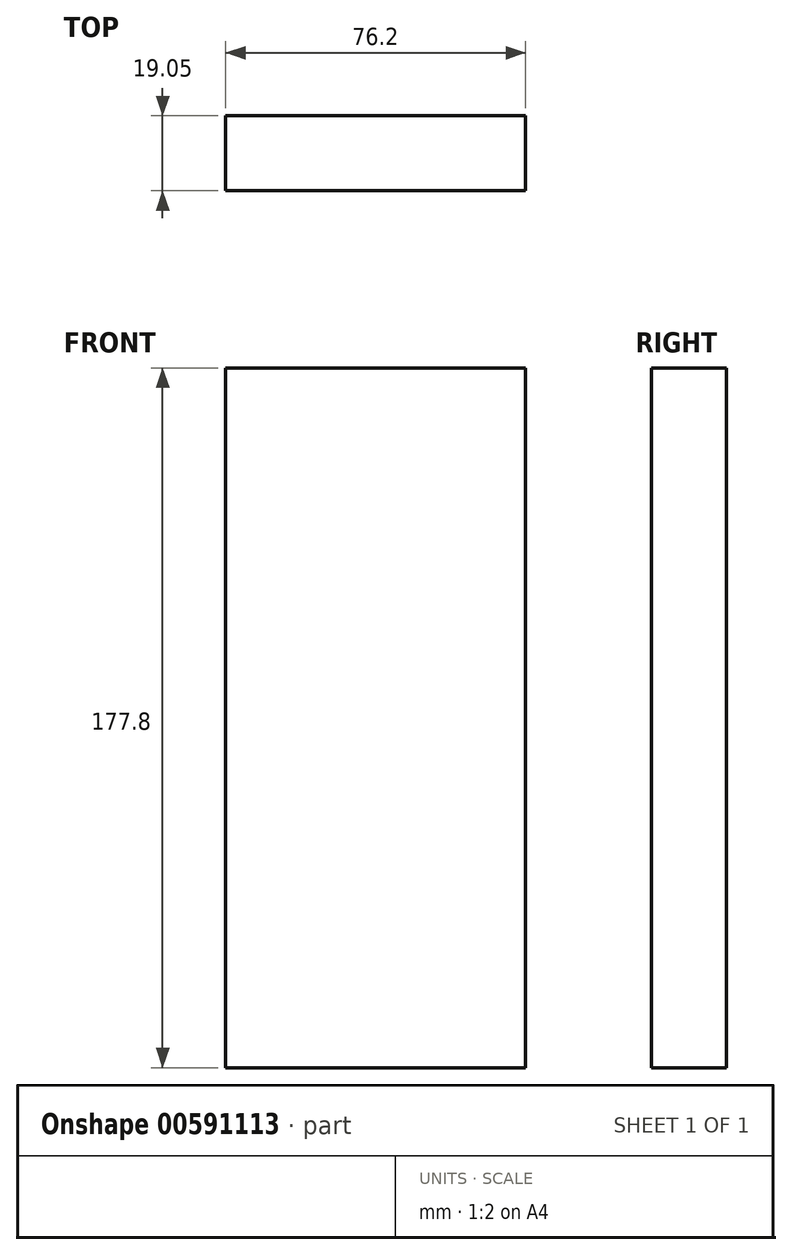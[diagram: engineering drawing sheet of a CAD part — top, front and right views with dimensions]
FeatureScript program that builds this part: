
annotation { "Feature Type Name" : "Feature", "Feature Type Description" : "" }
export const myFeature = defineFeature(function(context is Context, id is Id, definition is map)
    precondition{}
    {
        {
            var Q0;
            Q0=qCreatedBy(makeId("Front.planeOp"),FACE);
            var sketch = newSketch(context, id + "F0", { "sketchPlane" : qUnion([Q0])});
            skLineSegment(sketch, "E0.bottom", {"start": v(0, 0) * mm, "end": v(76.2, 0) * mm});
            skLineSegment(sketch, "E0.top", {"start": v(0, 177.8) * mm, "end": v(76.2, 177.8) * mm});
            skLineSegment(sketch, "E0.left", {"start": v(0, 0) * mm, "end": v(0, 177.8) * mm});
            skLineSegment(sketch, "E0.right", {"start": v(76.2, 0) * mm, "end": v(76.2, 177.8) * mm});
            skSolve(sketch);
        }
        {
            var Q0;
            Q0=makeQuery(id+"F0.imprint","IMPRINT",FACE,{"disambiguationData":[TD([[makeQuery(id+"F0.imprint","IMPRINT",EDGE,{"derivedFrom":sQuery(id+"F0.wireOp",EDGE,"E0.bottom")}),1.0]])]});
            extrude(context, id + "F1", {"entities" : qUnion([Q0]), "depth" : 19.05 * mm, "offsetDistance" : 25.4 * mm});
        }
    });
